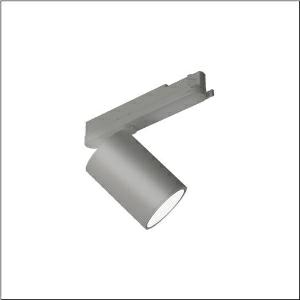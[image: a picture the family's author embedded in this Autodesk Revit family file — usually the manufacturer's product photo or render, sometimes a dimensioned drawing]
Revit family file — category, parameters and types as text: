
# Revit family: spot_31_51sf63mab4b
name_source: partatom
category: Lighting Fixtures
units: mm (PartAtom-declared; Revit-internal decimal feet)

## family parameters
Cut with Voids When Loaded = No
Host = Face
Light Source = No
Part Type = Normal
Room Calculation Point = No
Round Connector Dimension = Use Diameter
Shared = No

## types (1)
- --- (1 x LED, 5030 lm, 41.7 W, 3000K)
    Apparent Load = 42 VA
    CIE Flux Codes = 92 97 99 100 100
    Color Rendering = 90
    Color Temperature = 3000K
    Default Elevation = 1800 mm
    Description = Spot 31, directional spotlight, light control with lens, of PMMA, LED rated luminous flux: 4.830lm, light colour: 930, with 3-phase adapter, mains connection: 220..240V, AC, 50/60Hz, of aluminium, metallic grey (RAL 9006), length: 213mm, diameter: 90mm, protection rating (complete): IP20, insulation class (complete): insulation class I (protective earthing), certification: CE, impact resistance: IK02, permissible ambient temperature for indoor applications: -20..+40°C, packaging unit: 1 piece
    Height = 175 mm
    Lamp = 1 x LED
    Lamp Light Flux = 5030 lm
    Lamp Power = 41.7 W
    Lamp count = 1
    Length = 90 mm
    Luminous efficacy = 121 lm/W
    Manufacturer = Siteco
    ModVariant = No
    Model = 51SF63MAB4B
    Mounting Place = Ceiling
    Mounting Type = Pendant
    Number of Poles = 1
    OnlyDefault = Yes
    Power Factor = 1
    Product Name = Spot 31
    Product group = directional spotlight
    ProductGroupID = 905
    Protection Class = Protection class I
    Protection Degree = IP 20
    RLX_Detail_Level = 1
    RLX_Emergency_Light_Flux = 0 lm
    RLX_Emergency_Type = 0
    RLX_Emergency_Type_DB = No
    RlxData = <blob elided: 19985 chars, md5=d0577880>
    Socket = socket
    Standby Power = 0 W
    System Light Flux = 5030 lm
    System Power = 42 W
    Type Comments = factory setting: luminous flux: 100 % | (ON | ON | ON | ON) | 1050 mA
    Type Image = l_1273725.jpg
    URL = http://relux.com
    VarID = @adj_095987
    Voltage = 0 V
    Weight = 0.00 kg
    Width = 0 mm  [stored 0 ft]

note: [stored X ft] marks values corroborated as IEEE doubles in the binary element streams (Revit-internal decimal feet)

## geometry (parser evidence)
native form markers: Blend x4, Sweep x10
no freeform markers — native parametric forms only
